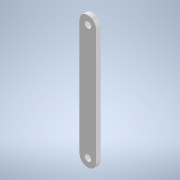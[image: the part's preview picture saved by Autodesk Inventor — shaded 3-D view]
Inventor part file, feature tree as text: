
AUTODESK INVENTOR PART (.ipt)
format: ipt  version: 2022 (Build 260153000, 153)  size: 107,008 bytes
history: native  units: mm
features: other x2, extrude x1, sketch x1, reference x1
ambient origin geometry x8: Origin, YZ Plane, XZ Plane, XY Plane, X Axis, Y Axis, Z Axis, Center Point
bodies: Solid1 (feature_tree)
feature tree (5):
  extrude  "Extrusion1"  Depth=3.2mm
  sketch  "Sketch1"  dims[d0=12.0mm d1=82.5mm d3=3.2mm d4=0.0mm]
  reference  "Reference1"
  other  "Caja_Reductora.iam"
  other  "Acople_TransPot:1"
